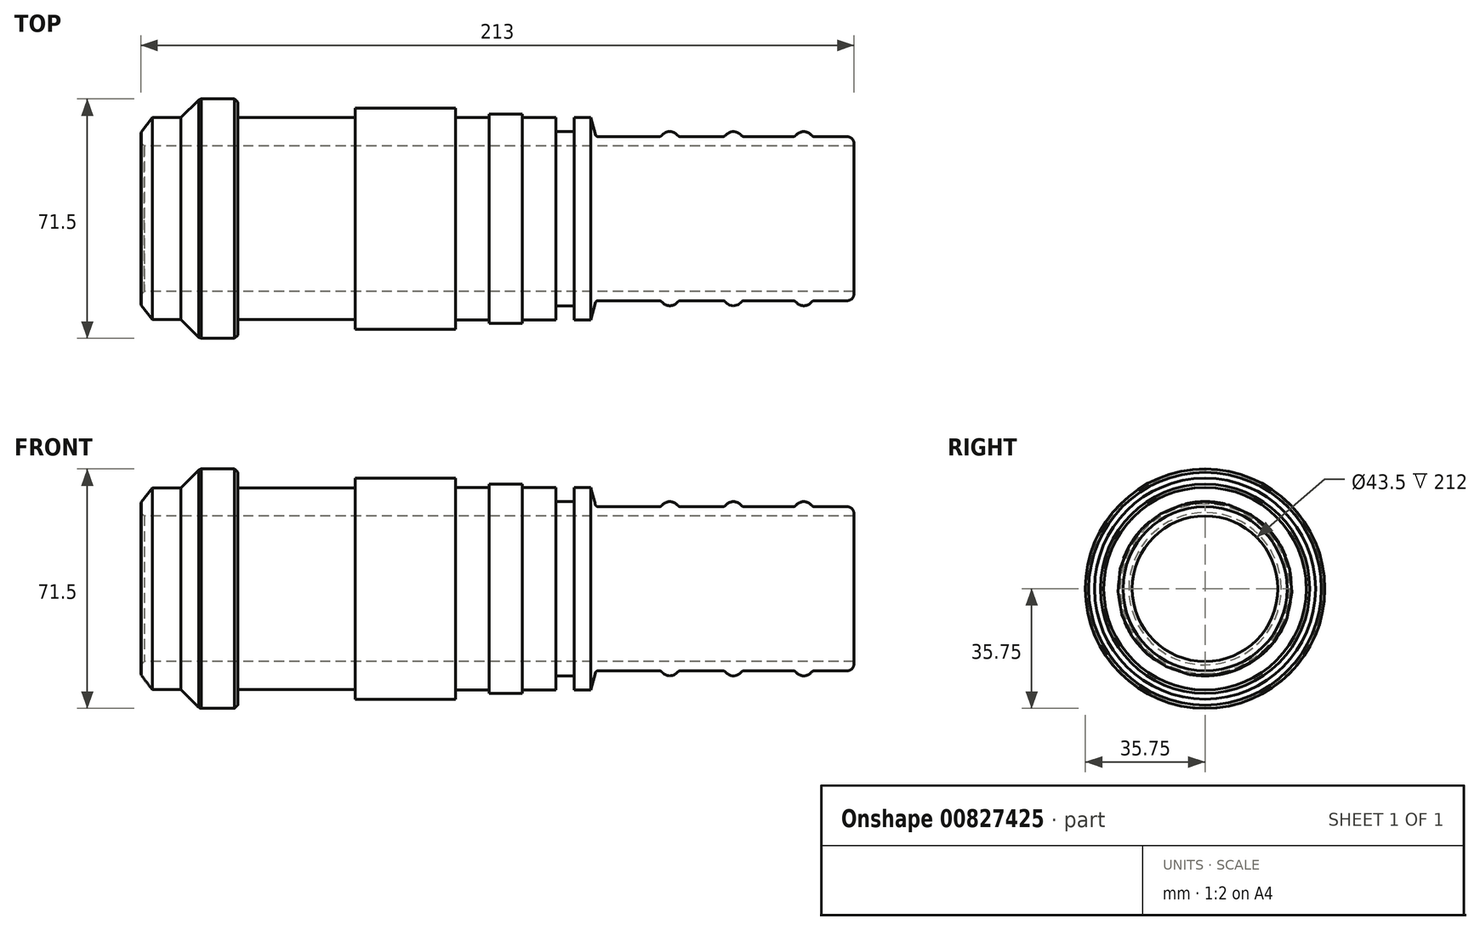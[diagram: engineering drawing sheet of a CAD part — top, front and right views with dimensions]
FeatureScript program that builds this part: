
annotation { "Feature Type Name" : "Feature", "Feature Type Description" : "" }
export const myFeature = defineFeature(function(context is Context, id is Id, definition is map)
    precondition{}
    {
        {
            var Q0;
            Q0=qCreatedBy(makeId("Front.planeOp"),FACE);
            var sketch = newSketch(context, id + "F0", { "sketchPlane" : qUnion([Q0])});
            skLineSegment(sketch, "E0", {"start": v(0, 0) * mm, "end": v(88.97, 0) * mm, "construction": true});
            skLineSegment(sketch, "E1", {"start": v(213, 21.75) * mm, "end": v(0, 21.75) * mm});
            skLineSegment(sketch, "E2", {"start": v(17.6, 35.75) * mm, "end": v(29, 35.75) * mm});
            skLineSegment(sketch, "E3", {"start": v(29, 35.75) * mm, "end": v(29, 30.15) * mm});
            skLineSegment(sketch, "E4", {"start": v(29, 30.15) * mm, "end": v(64, 30.15) * mm});
            skLineSegment(sketch, "E5", {"start": v(64, 30.15) * mm, "end": v(64, 33) * mm});
            skLineSegment(sketch, "E6", {"start": v(64, 33) * mm, "end": v(94, 33) * mm});
            skLineSegment(sketch, "E7", {"start": v(124, 30.25) * mm, "end": v(124, 26) * mm});
            skLineSegment(sketch, "E8", {"start": v(124, 26) * mm, "end": v(129.4, 26) * mm});
            skLineSegment(sketch, "E9", {"start": v(129.4, 26) * mm, "end": v(129.4, 30.25) * mm});
            skLineSegment(sketch, "E10", {"start": v(129.4, 30.25) * mm, "end": v(134.4, 30.25) * mm});
            skLineSegment(sketch, "E11", {"start": v(134.4, 30.25) * mm, "end": v(135.94, 24.5) * mm});
            skLineSegment(sketch, "E12", {"start": v(135.94, 24.5) * mm, "end": v(155.4, 24.5) * mm});
            skLineSegment(sketch, "E13.trimOffspring", {"start": v(0, 21.75) * mm, "end": v(0, 25.65) * mm});
            skArc(sketch, "E14", {"start": v(160.6, 24.5) * mm, "mid": v(158, 26) * mm, "end": v(155.4, 24.5) * mm});
            skArc(sketch, "E15", {"start": v(179.6, 24.5) * mm, "mid": v(177, 26) * mm, "end": v(174.4, 24.5) * mm});
            skArc(sketch, "E16", {"start": v(200.6, 24.5) * mm, "mid": v(198, 26) * mm, "end": v(195.4, 24.5) * mm});
            skLineSegment(sketch, "E17", {"start": v(213, 21.75) * mm, "end": v(213, 24.5) * mm});
            skLineSegment(sketch, "E18.trimOffspring", {"start": v(160.6, 24.5) * mm, "end": v(174.4, 24.5) * mm});
            skLineSegment(sketch, "E19.trimOffspring", {"start": v(179.6, 24.5) * mm, "end": v(195.4, 24.5) * mm});
            skLineSegment(sketch, "E20.trimOffspring", {"start": v(200.6, 24.5) * mm, "end": v(213, 24.5) * mm});
            skLineSegment(sketch, "E21", {"start": v(94, 33) * mm, "end": v(94, 30.25) * mm});
            skLineSegment(sketch, "E22", {"start": v(94, 30.25) * mm, "end": v(104, 30.25) * mm});
            skLineSegment(sketch, "E23", {"start": v(114, 30.25) * mm, "end": v(114, 31.25) * mm});
            skLineSegment(sketch, "E24", {"start": v(114, 31.25) * mm, "end": v(104, 31.25) * mm});
            skLineSegment(sketch, "E25", {"start": v(104, 31.25) * mm, "end": v(104, 30.25) * mm});
            skLineSegment(sketch, "E26.trimOffspring", {"start": v(114, 30.25) * mm, "end": v(124, 30.25) * mm});
            skLineSegment(sketch, "E27", {"start": v(17.6, 35.75) * mm, "end": v(12, 30.15) * mm});
            skLineSegment(sketch, "E28", {"start": v(12, 30.15) * mm, "end": v(3.45, 30.15) * mm});
            skPoint(sketch, "E29.orphan", {"position": v(0, 35.75) * mm});
            skLineSegment(sketch, "E30", {"start": v(3.45, 30.15) * mm, "end": v(0, 25.65) * mm});
            skSolve(sketch);
        }
        {
            var Q0;
            Q0=makeQuery(id+"F0.imprint","IMPRINT",FACE,{"disambiguationData":[TD([[makeQuery(id+"F0.imprint","IMPRINT",EDGE,{"derivedFrom":sQuery(id+"F0.wireOp",EDGE,"E1")}),-1.0]])]});
            var Q1;
            Q1=sQuery(id+"F0.wireOp",EDGE,"E0");
            revolve(context, id + "F1", {"surfaceOperationType" : NewSurfaceOperationType.NEW, "entities" : qUnion([Q0]), "axis" : qUnion([Q1]), "revolveType" : RevolveType.FULL});
        }
        {
            var Q0;
            Q0=makeQuery(id+"F1.opRevolve","SWEPT_EDGE",EDGE,{"disambiguationData":[OSD([sQuery(id+"F0.wireOp",EDGE,"E16"),sQuery(id+"F0.wireOp",EDGE,"E20.trimOffspring")])]});
            var Q1;
            Q1=makeQuery(id+"F1.opRevolve","SWEPT_EDGE",EDGE,{"disambiguationData":[OSD([sQuery(id+"F0.wireOp",EDGE,"E15"),sQuery(id+"F0.wireOp",EDGE,"E19.trimOffspring")])]});
            var Q2;
            Q2=makeQuery(id+"F1.opRevolve","SWEPT_EDGE",EDGE,{"disambiguationData":[OSD([sQuery(id+"F0.wireOp",EDGE,"E14"),sQuery(id+"F0.wireOp",EDGE,"E18.trimOffspring")])]});
            var Q3;
            Q3=makeQuery(id+"F1.opRevolve","SWEPT_EDGE",EDGE,{"disambiguationData":[OSD([sQuery(id+"F0.wireOp",EDGE,"E12"),sQuery(id+"F0.wireOp",EDGE,"E14")])]});
            var Q4;
            Q4=makeQuery(id+"F1.opRevolve","SWEPT_EDGE",EDGE,{"disambiguationData":[OSD([sQuery(id+"F0.wireOp",EDGE,"E15"),sQuery(id+"F0.wireOp",EDGE,"E18.trimOffspring")])]});
            var Q5;
            Q5=makeQuery(id+"F1.opRevolve","SWEPT_EDGE",EDGE,{"disambiguationData":[OSD([sQuery(id+"F0.wireOp",EDGE,"E16"),sQuery(id+"F0.wireOp",EDGE,"E19.trimOffspring")])]});
            fillet(context, id + "F2", {"entities" : qUnion([Q0, Q1, Q2, Q3, Q4, Q5]), "radius" : 1.2 * mm, "tangentPropagation" : true, "allowEdgeOverflow" : false});
        }
        {
            var Q0;
            Q0=makeQuery(id+"F1.opRevolve","SWEPT_EDGE",EDGE,{"disambiguationData":[OSD([sQuery(id+"F0.wireOp",EDGE,"E17"),sQuery(id+"F0.wireOp",EDGE,"E20.trimOffspring")])]});
            fillet(context, id + "F3", {"entities" : qUnion([Q0]), "radius" : 2 * mm, "tangentPropagation" : true, "allowEdgeOverflow" : false});
        }
        {
            var Q0;
            Q0=makeQuery(id+"F1.opRevolve","SWEPT_EDGE",EDGE,{"disambiguationData":[OSD([sQuery(id+"F0.wireOp",EDGE,"E11"),sQuery(id+"F0.wireOp",EDGE,"E12")])]});
            fillet(context, id + "F4", {"entities" : qUnion([Q0]), "radius" : .8 * mm, "tangentPropagation" : true, "allowEdgeOverflow" : false});
        }
        {
            var Q0;
            Q0=makeQuery(id+"F1.opRevolve","SWEPT_EDGE",EDGE,{"disambiguationData":[OSD([sQuery(id+"F0.wireOp",EDGE,"E7"),sQuery(id+"F0.wireOp",EDGE,"E8")])]});
            var Q1;
            Q1=makeQuery(id+"F1.opRevolve","SWEPT_EDGE",EDGE,{"disambiguationData":[OSD([sQuery(id+"F0.wireOp",EDGE,"E8"),sQuery(id+"F0.wireOp",EDGE,"E9")])]});
            fillet(context, id + "F5", {"entities" : qUnion([Q0, Q1]), "radius" : .4 * mm, "tangentPropagation" : true, "allowEdgeOverflow" : false});
        }
        {
            var Q0;
            Q0=makeQuery(id+"F1.opRevolve","SWEPT_EDGE",EDGE,{"disambiguationData":[OSD([sQuery(id+"F0.wireOp",EDGE,"E2"),sQuery(id+"F0.wireOp",EDGE,"E3")])]});
            var Q1;
            Q1=makeQuery(id+"F1.opRevolve","SWEPT_EDGE",EDGE,{"disambiguationData":[OSD([sQuery(id+"F0.wireOp",EDGE,"E2"),sQuery(id+"F0.wireOp",EDGE,"E13.trimOffspring")])]});
            chamfer(context, id + "F6", {"entities" : qUnion([Q0, Q1]), "width" : 1 * mm, "tangentPropagation" : true});
        }
    });
